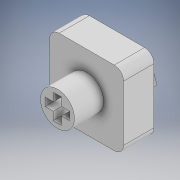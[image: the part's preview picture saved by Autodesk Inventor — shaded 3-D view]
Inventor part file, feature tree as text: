
AUTODESK INVENTOR PART (.ipt)
format: ipt  version: 2022 (Build 260153000, 153)  size: 242,688 bytes
history: native  units: in
note: dims shown in document units (in); Inventor stores cm internally (conversion verified against a paired STEP export)
features: sketch x4, extrude x3, plane x1, projected_geometry x1
ambient origin geometry x8: Origin, YZ Plane, XZ Plane, XY Plane, X Axis, Y Axis, Z Axis, Center Point
bodies: Body1 (feature_tree)
feature tree (9):
  sketch  "Sketch1"  dims[d3=0.2205in d4=0.1594in]
  plane  "Work Plane1"
  sketch  "Sketch2"  dims[d5=0.0531in d6=0.1594in]
  extrude  "Extrusion3"  Depth=0.1594in
  extrude  "Extrusion4"  Depth=0.1594in
  extrude  "Extrusion5"  Depth=0.5016in
  projected_geometry  "Projected Loop1"
  sketch  "Sketch3"  dims[d7=0.0531in d10=0.5016in]
  sketch  "Sketch4"  dims[d12=0.1969in d13=0.0in d14=0.2205in d15=0.1594in d16=0.0531in d17=0.1594in d18=0.0531in d19=0.189in d20=0.0in d23=0.0354in d24=0.0in]
